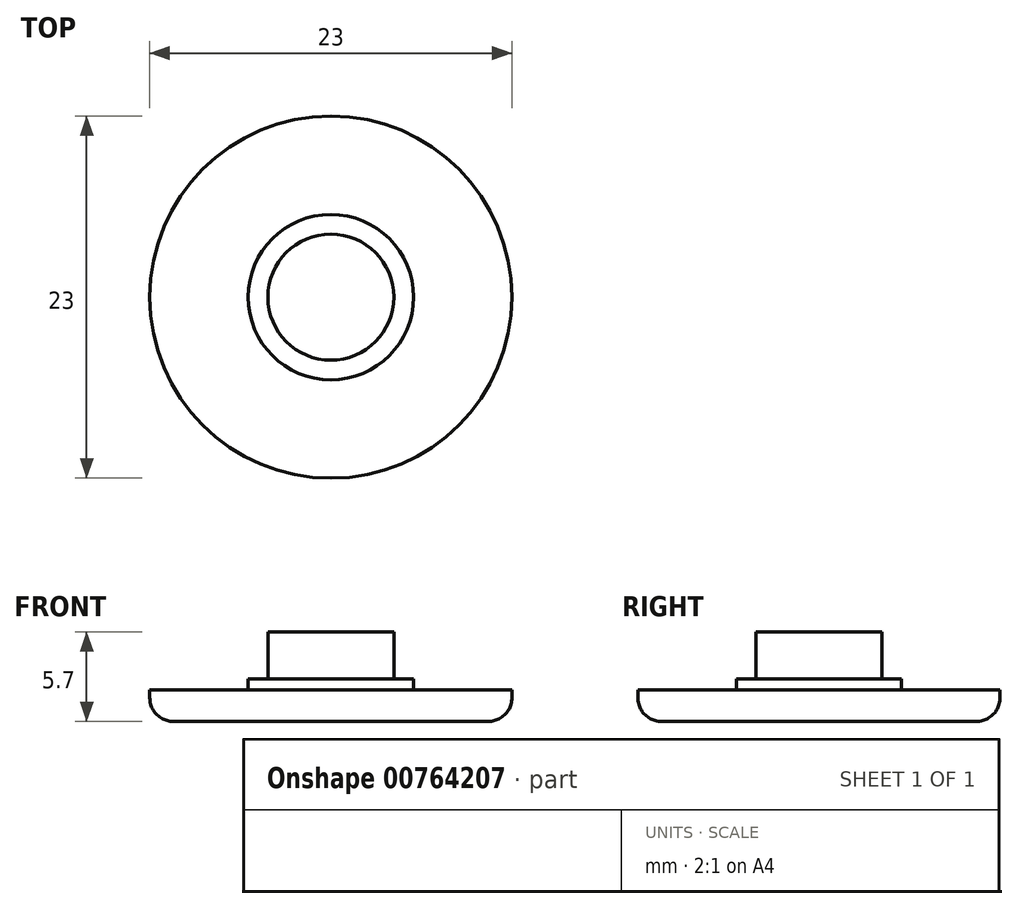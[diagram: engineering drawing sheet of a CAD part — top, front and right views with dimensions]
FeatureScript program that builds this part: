
annotation { "Feature Type Name" : "Feature", "Feature Type Description" : "" }
export const myFeature = defineFeature(function(context is Context, id is Id, definition is map)
    precondition{}
    {
        {
            var Q0;
            Q0=qCreatedBy(makeId("Top.planeOp"),FACE);
            var sketch = newSketch(context, id + "F0", { "sketchPlane" : qUnion([Q0])});
            skCircle(sketch, "E0", {"center": v(0, 0) * mm, "radius": 11.5 * mm});
            skSolve(sketch);
        }
        {
            var Q0;
            Q0 = qSketchRegion(id + "F0", true);
            extrude(context, id + "F1", {"entities" : qUnion([Q0]), "depth" : 2 * mm, "offsetDistance" : 25 * mm});
        }
        {
            var Q0;
            Q0=makeQuery(id+"F1.opExtrude","CAP_FACE",FACE,{"disambiguationData":[OSD([sQuery(id+"F0.wireOp",EDGE,"E0")])],"isStart":false});
            var sketch = newSketch(context, id + "F2", { "sketchPlane" : qUnion([Q0])});
            skCircle(sketch, "E1", {"center": v(0, 0) * mm, "radius": 5.25 * mm});
            skSolve(sketch);
        }
        {
            var Q0;
            Q0 = qSketchRegion(id + "F2", true);
            extrude(context, id + "F3", {"entities" : qUnion([Q0]), "operationType" : NewBodyOperationType.ADD, "depth" : 0.7 * mm, "offsetDistance" : 25 * mm});
        }
        {
            var Q0;
            Q0=makeQuery(id+"F3.opExtrude","CAP_FACE",FACE,{"disambiguationData":[OSD([sQuery(id+"F2.wireOp",EDGE,"E1")])],"isStart":false});
            var sketch = newSketch(context, id + "F4", { "sketchPlane" : qUnion([Q0])});
            skCircle(sketch, "E2", {"center": v(0, 0) * mm, "radius": 4 * mm});
            skSolve(sketch);
        }
        {
            var Q0;
            Q0 = qSketchRegion(id + "F4", true);
            extrude(context, id + "F5", {"entities" : qUnion([Q0]), "operationType" : NewBodyOperationType.ADD, "depth" : 3 * mm, "offsetDistance" : 25 * mm});
        }
        {
            var Q0;
            Q0=makeQuery(id+"F1.opExtrude","CAP_EDGE",EDGE,{"disambiguationData":[OSD([sQuery(id+"F0.wireOp",EDGE,"E0")])],"isStart":true});
            fillet(context, id + "F6", {"entities" : qUnion([Q0]), "radius" : 1.5 * mm, "tangentPropagation" : true, "allowEdgeOverflow" : false});
        }
    });
